# Revit family: Stayhot Värmehäll WP 405 RE_Reglerbar
name_source: partatom
category: Specialty Equipment
units: mm (PartAtom-declared; Revit-internal decimal feet)

## family parameters
Always vertical = Yes
Cut with Voids When Loaded = No
Part Type = Normal
Room Calculation Point = No
Round Connector Dimension = Use Diameter
Shared = No
Work Plane-Based = No

## types (1)
- Stayhot Värmehäll WP 405 RE / Reglerbar
    Body Material = Stainless Steel
    Breadth = 720 mm  [stored 2.3622 ft]
    Default Elevation = 0 mm  [stored 0 ft]
    Depth = 425 mm  [stored 1.39436 ft]
    Description = Stayhot Värmehäll WP 405 RE / Reglerbar
    Display Material = Brown Glass
    Handle Material = Black Stainless Steel
    Height = 40 mm  [stored 0.131234 ft]
    Knob Material = Black Plastic
    Leg Material = Black Plastic
    Model = WP-405-RE
    Surface Material = Black Glass
    Voltage = 230 V
    Wattage = 400 W

note: [stored X ft] marks values corroborated as IEEE doubles in the binary element streams (Revit-internal decimal feet)

## geometry (parser evidence)
native form markers: Sweep x2
no freeform markers — native parametric forms only
